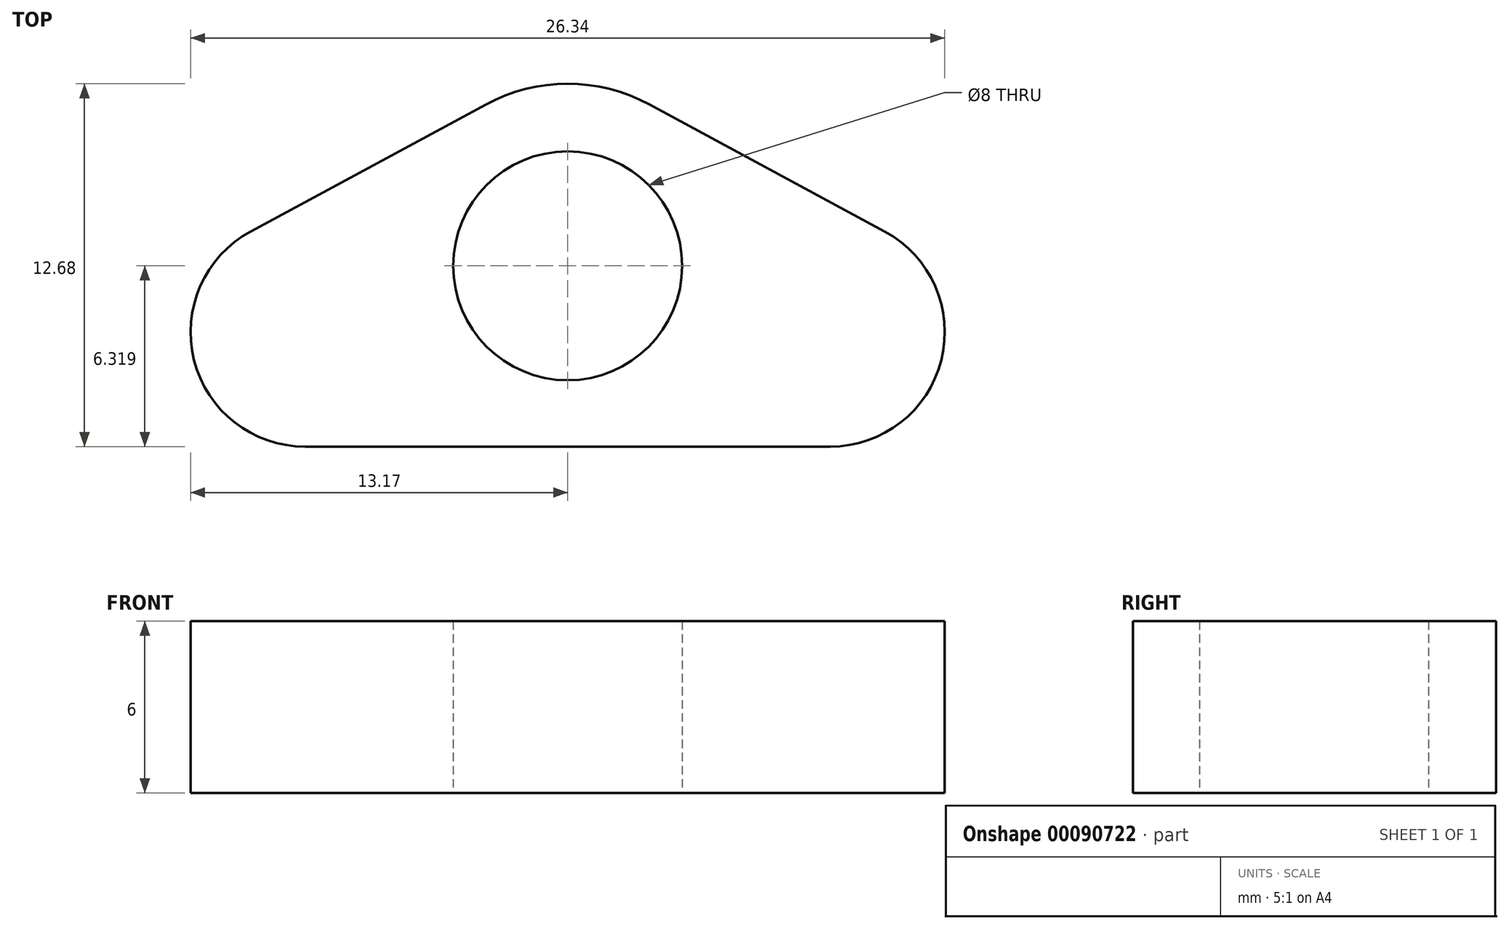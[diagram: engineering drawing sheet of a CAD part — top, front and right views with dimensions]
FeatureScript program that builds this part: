
annotation { "Feature Type Name" : "Feature", "Feature Type Description" : "" }
export const myFeature = defineFeature(function(context is Context, id is Id, definition is map)
    precondition{}
    {
        {
            var Q0;
            Q0=qCreatedBy(makeId("Top.planeOp"),FACE);
            var sketch = newSketch(context, id + "F0", { "sketchPlane" : qUnion([Q0])});
            skLineSegment(sketch, "E0", {"start": v(-25, 0) * mm, "end": v(25, 0) * mm});
            skLineSegment(sketch, "E1", {"start": v(25, 0) * mm, "end": v(0, 13.5) * mm});
            skLineSegment(sketch, "E2", {"start": v(0, 13.5) * mm, "end": v(-25, 0) * mm});
            skSolve(sketch);
        }
        {
            var Q0;
            Q0=makeQuery(id+"F0.imprint","IMPRINT",FACE,{"disambiguationData":[TD([[makeQuery(id+"F0.imprint","IMPRINT",EDGE,{"derivedFrom":sQuery(id+"F0.wireOp",EDGE,"E0")}),1.0]])]});
            extrude(context, id + "F1", {"entities" : qUnion([Q0]), "depth" : 6 * mm});
        }
        {
            var Q0;
            Q0=makeQuery(id+"F1.opExtrude","SWEPT_EDGE",EDGE,{"disambiguationData":[OSD([sQuery(id+"F0.wireOp",EDGE,"E0"),sQuery(id+"F0.wireOp",EDGE,"E1")])]});
            var Q1;
            Q1=makeQuery(id+"F1.opExtrude","SWEPT_EDGE",EDGE,{"disambiguationData":[OSD([sQuery(id+"F0.wireOp",EDGE,"E0"),sQuery(id+"F0.wireOp",EDGE,"E2")])]});
            fillet(context, id + "F2", {"entities" : qUnion([Q0, Q1]), "radius" : 4 * mm, "tangentPropagation" : true, "allowEdgeOverflow" : false});
        }
        {
            var Q0;
            Q0=makeQuery(id+"F1.opExtrude","SWEPT_EDGE",EDGE,{"disambiguationData":[OSD([sQuery(id+"F0.wireOp",EDGE,"E1"),sQuery(id+"F0.wireOp",EDGE,"E2")])]});
            fillet(context, id + "F3", {"entities" : qUnion([Q0]), "radius" : 6 * mm, "tangentPropagation" : true, "allowEdgeOverflow" : false});
        }
        {
            var Q0;
            Q0=qCreatedBy(makeId("Top.planeOp"),FACE);
            var sketch = newSketch(context, id + "F4", { "sketchPlane" : qUnion([Q0])});
            skCircle(sketch, "E3", {"center": v(0, 6.32) * mm, "radius": 4 * mm});
            skLineSegment(sketch, "E4", {"start": v(0, 6.32) * mm, "end": v(-3, 11.88) * mm, "construction": true});
            skLineSegment(sketch, "E5", {"start": v(3, 11.88) * mm, "end": v(0, 6.32) * mm, "construction": true});
            skLineSegment(sketch, "E6", {"start": v(0, 6.32) * mm, "end": v(0, 0) * mm, "construction": true});
            skSolve(sketch);
        }
        {
            var Q0;
            Q0 = qSketchRegion(id + "F4", true);
            extrude(context, id + "F5", {"entities" : qUnion([Q0]), "operationType" : NewBodyOperationType.REMOVE, "endBound" : BoundingType.THROUGH_ALL, "depth" : 25 * mm});
        }
    });
